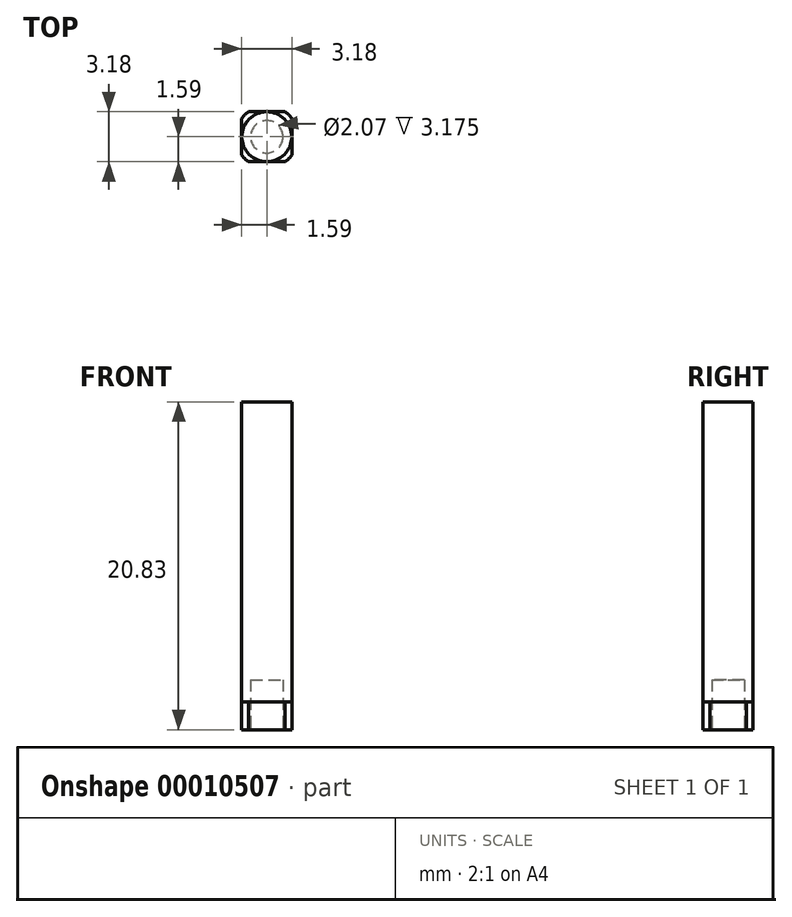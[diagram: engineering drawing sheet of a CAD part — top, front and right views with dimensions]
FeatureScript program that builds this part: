
annotation { "Feature Type Name" : "Feature", "Feature Type Description" : "" }
export const myFeature = defineFeature(function(context is Context, id is Id, definition is map)
    precondition{}
    {
        {
            var Q0;
            Q0=qCreatedBy(makeId("Top.planeOp"),FACE);
            var sketch = newSketch(context, id + "F0", { "sketchPlane" : qUnion([Q0])});
            skLineSegment(sketch, "E0.rect.bottom", {"start": v(1.16, 1.59) * mm, "end": v(-1.16, 1.59) * mm});
            skLineSegment(sketch, "E0.rect.top", {"start": v(1.16, -1.59) * mm, "end": v(-1.16, -1.59) * mm});
            skLineSegment(sketch, "E0.rect.left", {"start": v(1.59, 1.16) * mm, "end": v(1.59, -1.16) * mm});
            skLineSegment(sketch, "E0.rect.right", {"start": v(-1.59, 1.16) * mm, "end": v(-1.59, -1.16) * mm});
            skPoint(sketch, "E0.rect.middle", {"position": v(0, 0) * mm});
            skArc(sketch, "E1", {"start": v(-1.16, 1.59) * mm, "mid": v(-1.4, 1.4) * mm, "end": v(-1.59, 1.16) * mm});
            skPoint(sketch, "E2.orphan", {"position": v(1.59, 1.59) * mm});
            skPoint(sketch, "E3.orphan", {"position": v(-1.59, 1.59) * mm});
            skArc(sketch, "E4.trimOffspring", {"start": v(-1.59, -1.16) * mm, "mid": v(-1.4, -1.4) * mm, "end": v(-1.16, -1.59) * mm});
            skPoint(sketch, "E5.orphan", {"position": v(-1.59, -1.59) * mm});
            skArc(sketch, "E6.trimOffspring", {"start": v(1.16, -1.59) * mm, "mid": v(1.4, -1.4) * mm, "end": v(1.59, -1.16) * mm});
            skPoint(sketch, "E7.orphan", {"position": v(1.59, -1.59) * mm});
            skArc(sketch, "E8.trimOffspring", {"start": v(1.59, 1.16) * mm, "mid": v(1.4, 1.4) * mm, "end": v(1.16, 1.59) * mm});
            skSolve(sketch);
        }
        {
            var Q0;
            Q0 = qSketchRegion(id + "F0", true);
            extrude(context, id + "F1", {"entities" : qUnion([Q0]), "depth" : ((1 + 7 / 8) - 3 / 32) * mm});
        }
        {
            var Q0;
            Q0=makeQuery(id+"F1.opExtrude","CAP_FACE",FACE,{"disambiguationData":[OSD([sQuery(id+"F0.wireOp",EDGE,"E0.rect.bottom"),sQuery(id+"F0.wireOp",EDGE,"E0.rect.top"),sQuery(id+"F0.wireOp",EDGE,"E0.rect.left"),sQuery(id+"F0.wireOp",EDGE,"E0.rect.right"),sQuery(id+"F0.wireOp",EDGE,"E1"),sQuery(id+"F0.wireOp",EDGE,"E4.trimOffspring"),sQuery(id+"F0.wireOp",EDGE,"E6.trimOffspring"),sQuery(id+"F0.wireOp",EDGE,"E8.trimOffspring")])],"isStart":false});
            var sketch = newSketch(context, id + "F2", { "sketchPlane" : qUnion([Q0])});
            skCircle(sketch, "E9", {"center": v(0, 0) * mm, "radius": 1.59 * mm});
            skSolve(sketch);
        }
        {
            var Q0;
            Q0 = qSketchRegion(id + "F2", true);
            extrude(context, id + "F3", {"entities" : qUnion([Q0]), "operationType" : NewBodyOperationType.ADD, "depth" : 19.05 * mm});
        }
        {
            var Q0;
            Q0=makeQuery(id+"F1.opExtrude","CAP_FACE",FACE,{"disambiguationData":[OSD([sQuery(id+"F0.wireOp",EDGE,"E0.rect.bottom"),sQuery(id+"F0.wireOp",EDGE,"E0.rect.top"),sQuery(id+"F0.wireOp",EDGE,"E0.rect.left"),sQuery(id+"F0.wireOp",EDGE,"E0.rect.right"),sQuery(id+"F0.wireOp",EDGE,"E1"),sQuery(id+"F0.wireOp",EDGE,"E4.trimOffspring"),sQuery(id+"F0.wireOp",EDGE,"E6.trimOffspring"),sQuery(id+"F0.wireOp",EDGE,"E8.trimOffspring")])],"isStart":true});
            var sketch = newSketch(context, id + "F4", { "sketchPlane" : qUnion([Q0])});
            skCircle(sketch, "E10", {"center": v(0, 0) * mm, "radius": 1.03 * mm});
            skSolve(sketch);
        }
        {
            var Q0;
            Q0 = qSketchRegion(id + "F4", true);
            extrude(context, id + "F5", {"entities" : qUnion([Q0]), "operationType" : NewBodyOperationType.REMOVE, "oppositeDirection" : true, "depth" : 3.17 * mm});
        }
    });
